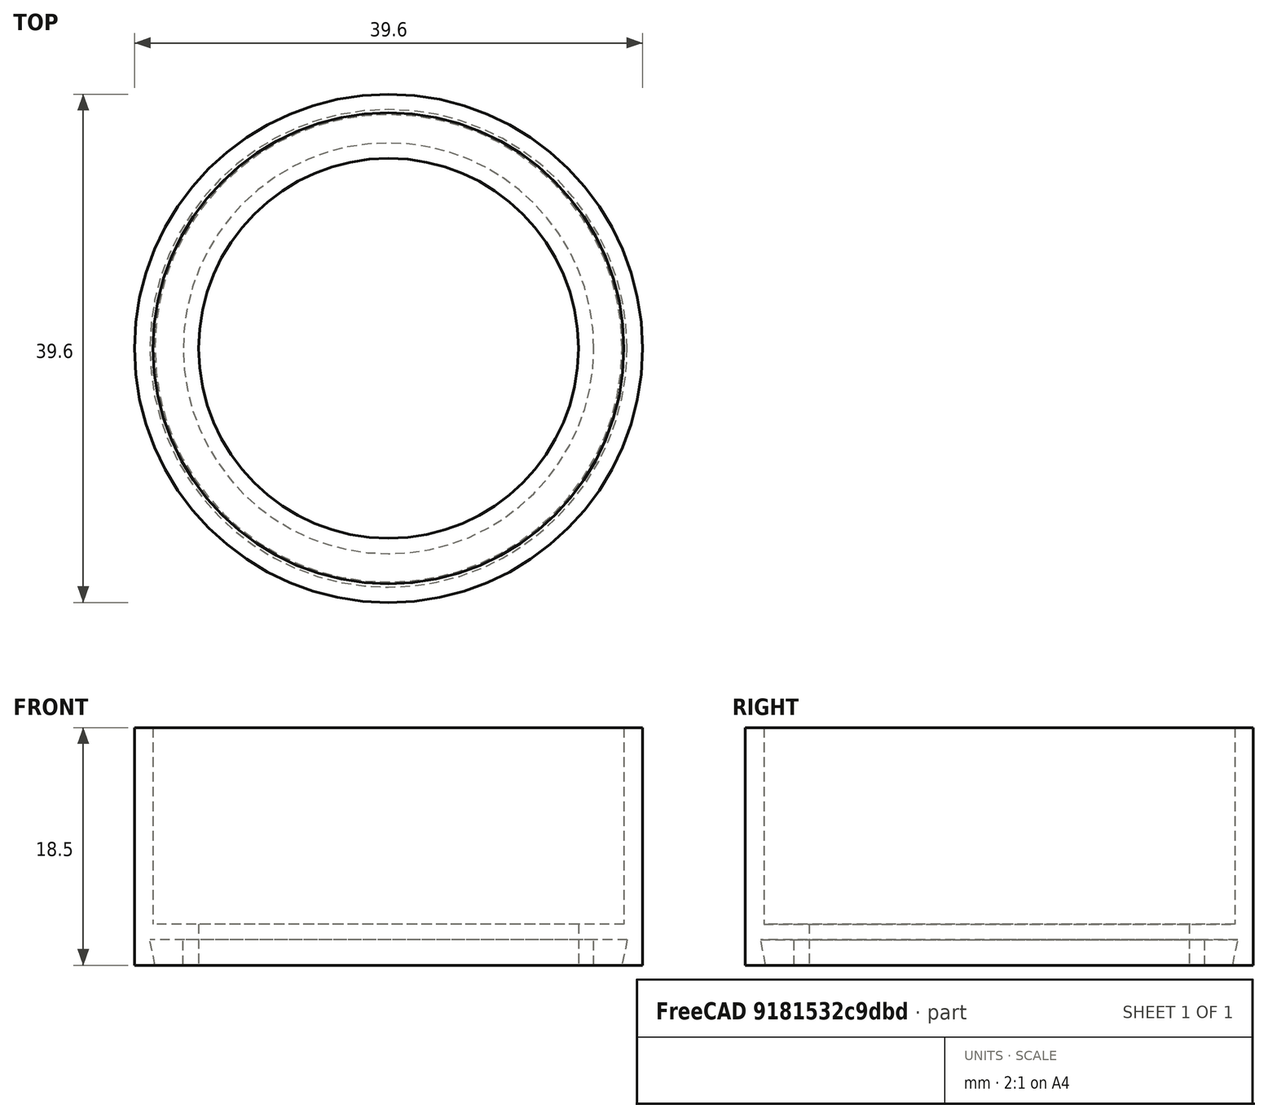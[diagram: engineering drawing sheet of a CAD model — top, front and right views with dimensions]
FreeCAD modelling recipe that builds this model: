
FCSTD DOCUMENT  (FreeCAD 0.20R29603 (Git))
Label: Kaarshouder
License: All rights reserved
LicenseURL: http://en.wikipedia.org/wiki/All_rights_reserved
objects: Sketcher::SketchObject×1, Spreadsheet::Sheet×1, PartDesign::Revolution×1, PartDesign::Body×1
note: 4 computed .brp shape members not serialized (recipe doc carries the construction recipe); baked Part::Feature solids carry a one-line shape summary decoded from their .brp

FEATURE [Sketcher::SketchObject] Sketch
  FullyConstrained = true
  Placement = pos=(0,0,0) rot=(1,0,0;1.5708rad)
  expr: Constraints[21] = <<dimensions>>.wall
  expr: Constraints[25] = <<dimensions>>.wall
  expr: Constraints[27] = <<dimensions>>.outerrim_r
  expr: Constraints[29] = <<dimensions>>.wall
  sketch-geometry (10):
    g0: LineSegment StartX=16 StartY=0 StartZ=0 EndX=16 EndY=2 EndZ=0
    g1: LineSegment StartX=16 StartY=2 StartZ=0 EndX=18.6 EndY=2 EndZ=0
    g2: LineSegment StartX=18.6 StartY=2 StartZ=0 EndX=18.2 EndY=0 EndZ=0
    g3: LineSegment StartX=18.2 StartY=0 StartZ=0 EndX=19.8 EndY=0 EndZ=0
    g4: LineSegment StartX=19.8 StartY=0 StartZ=0 EndX=19.8 EndY=18.5 EndZ=0
    g5: LineSegment StartX=19.8 StartY=18.5 StartZ=0 EndX=18.35 EndY=18.5 EndZ=0
    g6: LineSegment StartX=18.35 StartY=18.5 StartZ=0 EndX=18.35 EndY=3.2 EndZ=0
    g7: LineSegment StartX=18.35 StartY=3.2 StartZ=0 EndX=14.8 EndY=3.2 EndZ=0
    g8: LineSegment StartX=14.8 StartY=3.2 StartZ=0 EndX=14.8 EndY=0 EndZ=0
    g9: LineSegment StartX=14.8 StartY=0 StartZ=0 EndX=16 EndY=0 EndZ=0
  constraints (30):
    c: PointOnObject(g0,g-1)
    c: Vertical(g0)
    c: Coincident(g0,g1)
    c: Horizontal(g1)
    c: Coincident(g1,g2)
    c: PointOnObject(g2,g-1)
    c: Coincident(g2,g3)
    c: Horizontal(g3)
    c: Coincident(g3,g4)
    c: Vertical(g4)
    c: Coincident(g4,g5)
    c: Horizontal(g5)
    c: Coincident(g5,g6)
    c: Vertical(g6)
    c: Coincident(g6,g7)
    c: Horizontal(g7)
    c: Coincident(g7,g8)
    c: PointOnObject(g8,g-1)
    c: Vertical(g8)
    c: Coincident(g8,g9)
    c: Coincident(g9,g0)
    c: DistanceY(g0,g7) = 1.2
    c: DistanceY(g3,g1) = 2
    c: DistanceX(g-1,g0) = 16
    c: DistanceX(g-1,g5) = 18.35
    c: DistanceX(g7,g0) = 1.2
    c: DistanceX(g-1,g1) = 18.6
    c: DistanceX(g-1,g2) = 18.2
    c: DistanceY(g6,g5) = 15.3
    c: DistanceX(g1,g3) = 1.2
FEATURE [Spreadsheet::Sheet] Spreadsheet  label="dimensions"
  cells = A1=wall; B1(wall)=1.2; A2=innerrim_r; B2(innerrim_r)=16; A3=outerrim_r; B3(outerrim_r)=18.2; A4=outerrim_high_r; B4(outerrim_high_r)=18.6; A5=rim_height; B5(rim_height)=2; A7=light_hole_r; B7(light_hole_r)=6; A8=cap_height; B8(cap_height)=6
FEATURE [PartDesign::Revolution] Revolution
  Angle = 360
  Axis = (0,2e-16,1)
  Base = (0,0,0)
  Placement = pos=(0,0,0) rot=(1,0,0;1.5708rad)
  Profile = -> Sketch
  ReferenceAxis = -> Sketch [V_Axis]
  Reversed = true
FEATURE [PartDesign::Body] Body  label="kaarshouder"
  Group = -> [Sketch,Revolution]
  Origin = -> Origin
  Tip = -> Revolution
